# Revit family: Shower-Valve_Trim-KOHLER-MEMOIRS-K-99966T
name_source: partatom
category: Plumbing Fixtures
revit_build: Autodesk Revit 2017 (Build: 20160225_1515(x64)
units: mm (PartAtom-declared; Revit-internal decimal feet)

## family parameters
Cut with Voids When Loaded = No
Host = Face
OmniClass Number = 23.31.25.00
OmniClass Title = Toilet and Bath Specialties
Part Type = Normal
Room Calculation Point = No
Round Connector Dimension = Use Diameter
Shared = No

## types (12) — shared parameters
ADA Compliant = No
Assembly Code = D2010700
CW Connection = Yes
Cold Water Inlet = Cold Water Inlet
Date Modified = 10/20/2020
Default Elevation = 42"
Drain Included = No
Flow Rate = 0 GPM
HW Connection = Yes
Height = 7 1/16"
Hot Water Inlet = Hot Water Inlet
Manufacturer = KOHLER Co.
Master Format 2014 = 22 42 23
Master Format 2014 Name = Residential Showers
Material = Premium Metal Construction
Pressure = 72.52 psi
Product Documentation Link = https://files.kohler.com.cn
Product Name = MEMOIRS
Product Page URL = https://www.kohler.com.cn
Tempered Water Outlet 1 = Tempered Water Outlet 1
Tempered Water Outlet 2 = Tempered Water Outlet 2
URL = http://www.kohler.com.cn
Vent Connection = No
Waste Connection = No
Waste Water Outlet = Waste Water Outlet
WaterSense Certified = No
Width = 5 1/2"

## per-type parameters (varying)
| type | Description | Finish | Length | Mema Cross Handle | Mema Lever Handle | Model | Type |
| Mema Cross Handle, CP- Polished Chrome | Smart formula into the wall heated bathtub rain shower valve core and panel - classic type (Mema cross handle) | Kohler-Metal-CP-Polished_Chrome | 4 1/8" | Yes | No | K-99966T-3S-CP | 1 |
| Mema Rod Handle, CP- Polished Chrome | Smart formula into the wall-mounted heated bathtub rain shower valve core and panel - classic type (Merma rod handle) | Kohler-Metal-CP-Polished_Chrome | 4 1/4" | No | Yes | K-99966T-4V-CP | 7 |
| Mema cross Handle, AF-Flange gold | Smart formula into the wall heated bathtub rain shower valve core and panel - classic type (Mema cross handle) | Kohler-Metal-AF-Flange_Gold | 4 1/8" | Yes | No | K-99966T-3S-AF | 2 |
| Mema Cross Handle,BN- Romen silver | Smart formula into the wall heated bathtub rain shower valve core and panel - classic type (Mema cross handle) | Kohler-Metal-BN-Roman_Silver | 4 1/8" | Yes | No | K-99966T-3S-BN | 3 |
| Mema Cross Handle, SN-Champagne gold | Smart formula into the wall heated bathtub rain shower valve core and panel - classic type (Mema cross handle) | Kohler-Metal-SN-Champagne_Gold | 4 1/8" | Yes | No | K-99966T-3S-SN | 4 |
| Mema Cross Handle,RGD-Rose gold | Smart formula into the wall heated bathtub rain shower valve core and panel - classic type (Mema cross handle) | Kohler-Metal-RGD-Rose_Gold | 4 1/8" | Yes | No | K-99966T-3S-RGD | 5 |
| Mema Cross Handle, BL-Matte black | Smart formula into the wall heated bathtub rain shower valve core and panel - classic type (Mema cross handle) | Kohler-Metal-BL-Matte_Black | 4 1/8" | Yes | No | K-99966T-3S-BL | 6 |
| Mema Rod Handle,AF-FLange gold | Smart formula into the wall-mounted heated bathtub rain shower valve core and panel - classic type (Merma rod handle) | Kohler-Metal-AF-Flange_Gold | 4 1/4" | No | Yes | K-99966T-4V-AF | 8 |
| Mema Rod Handle, BN- Romen silver | Smart formula into the wall-mounted heated bathtub rain shower valve core and panel - classic type (Merma rod handle) | Kohler-Metal-BN-Roman_Silver | 4 1/4" | No | Yes | K-99966T-4V-BN | 9 |
| Mema Rod Handle,SN-Champagne gold | Smart formula into the wall-mounted heated bathtub rain shower valve core and panel - classic type (Merma rod handle) | Kohler-Metal-SN-Champagne_Gold | 4 1/4" | No | Yes | K-99966T-4V-SN | 10 |
| Mema Rod Handle, RGD- Rose gold | Smart formula into the wall-mounted heated bathtub rain shower valve core and panel - classic type (Merma rod handle) | Kohler-Metal-RGD-Rose_Gold | 4 1/4" | No | Yes | K-99966T-4V-RGD | 11 |
| Mema Rod Handle, BL- Matte black | Smart formula into the wall-mounted heated bathtub rain shower valve core and panel - classic type (Merma rod handle) | Kohler-Metal-BL-Matte_Black | 4 1/4" | No | Yes | K-99966T-4V-BL | 12 |

## geometry (parser evidence)
native form markers: Sweep x6
no freeform markers — native parametric forms only
